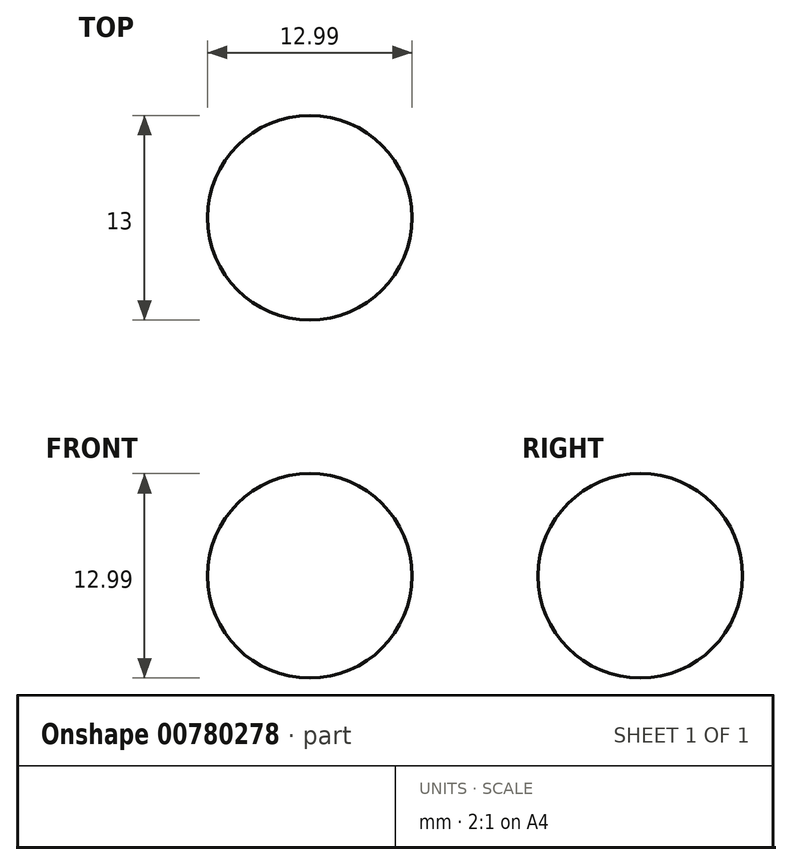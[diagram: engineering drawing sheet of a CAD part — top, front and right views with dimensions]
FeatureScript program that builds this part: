
annotation { "Feature Type Name" : "Feature", "Feature Type Description" : "" }
export const myFeature = defineFeature(function(context is Context, id is Id, definition is map)
    precondition{}
    {
        {
            var Q0;
            Q0=qCreatedBy(makeId("Front.planeOp"),FACE);
            var sketch = newSketch(context, id + "F0", { "sketchPlane" : qUnion([Q0])});
            skCircle(sketch, "E0", {"center": v(-16.11, -8.2) * mm, "radius": 6.5 * mm});
            skLineSegment(sketch, "E1", {"start": v(-22.6, -8.2) * mm, "end": v(-9.62, -8.2) * mm});
            skSolve(sketch);
        }
        {
            var Q0;
            {var subQ0=sQuery(id+"F0.wireOp",EDGE,"E1");Q0=makeQuery(id+"F0.imprint","IMPRINT",FACE,{"disambiguationData":[TD([[makeQuery(id+"F0.imprint","IMPRINT",EDGE,{"derivedFrom":subQ0}),1.0]])]});}
            var Q1;
            Q1=sQuery(id+"F0.wireOp",EDGE,"E1");
            revolve(context, id + "F1", {"surfaceOperationType" : NewSurfaceOperationType.NEW, "entities" : qUnion([Q0]), "axis" : qUnion([Q1]), "revolveType" : RevolveType.FULL});
        }
    });
